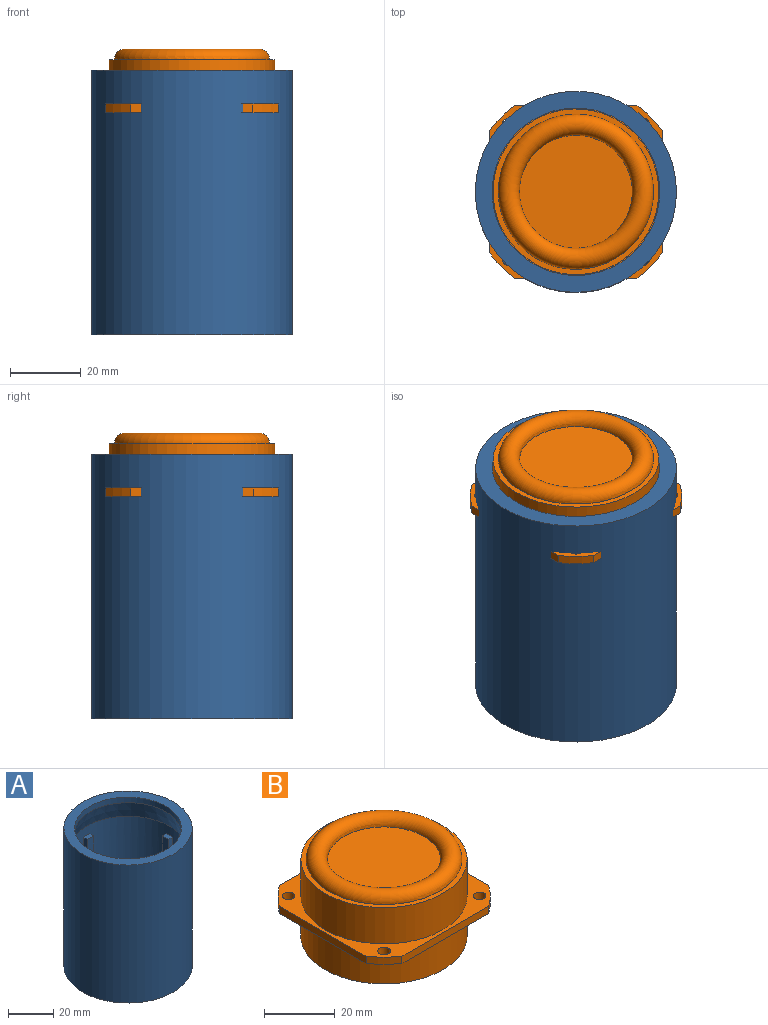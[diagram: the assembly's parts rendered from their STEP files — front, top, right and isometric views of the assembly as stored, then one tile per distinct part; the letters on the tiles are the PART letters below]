
ASSEMBLY  parts=2 mates=1
PART A: 32 faces, bbox 57x57x75 mm
  f0: plane 30x4mm, normal (1,0,0), area 120mm2, adj f5,f10,f11,f28
  f1: plane 30x4mm, normal (0,-1,0), area 120mm2, adj f5,f13,f14,f26
  f2: plane 30x4mm, normal (-1,0,0), area 120mm2, adj f5,f16,f17,f24
  f3: plane 30x4mm, normal (0,1,0), area 120mm2, adj f5,f19,f20,f22
  f4: cylinder r=26mm len=60mm, axis (0,0,-1), area 8920.9mm2, adj f5,f9,f10,f11,f12,f13,f14,f15
  f5: plane 51.85x51.85mm, normal (0,0,1), area 1935.6mm2, adj f0,f1,f2,f3,f4,f7,f10,f11
  f6: cylinder r=28.5mm len=75mm, axis (0,0,-1), area 13430.3mm2, adj f8,f30
  f7: cylinder r=2mm len=4mm, axis (0,0,1), area 37.7mm2, adj f5,f8
  f8: plane 57x57mm, normal (0,0,-1), area 2539.2mm2, adj f6,f7
  f9: plane 4x2.5mm, normal (0,0,1), area 9.9mm2, adj f4,f10,f11,f27
  f10: plane 55x10.92mm, normal (0,-1,0), area 388.3mm2, adj f0,f4,f5,f9,f27,f28
  f11: plane 55x10.92mm, normal (0,1,0), area 388.3mm2, adj f0,f4,f5,f9,f27,f28
  f12: plane 4x2.5mm, normal (0,0,1), area 9.9mm2, adj f4,f13,f14,f25
  f13: plane 55x10.92mm, normal (1,0,0), area 388.3mm2, adj f1,f4,f5,f12,f25,f26
  f14: plane 55x10.92mm, normal (-1,0,0), area 388.3mm2, adj f1,f4,f5,f12,f25,f26
  f15: plane 4x2.5mm, normal (0,0,1), area 9.9mm2, adj f4,f16,f17,f23
  f16: plane 55x10.92mm, normal (0,-1,0), area 388.3mm2, adj f2,f4,f5,f15,f23,f24
  f17: plane 55x10.92mm, normal (0,1,0), area 388.3mm2, adj f2,f4,f5,f15,f23,f24
  f18: plane 4x2.5mm, normal (0,0,1), area 9.9mm2, adj f4,f19,f20,f21
  f19: plane 55x10.92mm, normal (-1,0,0), area 388.3mm2, adj f3,f4,f5,f18,f21,f22
  f20: plane 55x10.92mm, normal (1,0,0), area 388.3mm2, adj f3,f4,f5,f18,f21,f22
  f21: plane 25x4mm, normal (0,1,0), area 100mm2, adj f18,f19,f20,f22
  f22: plane 8.5x4mm, normal (0,0,1), area 34mm2, adj f3,f19,f20,f21
  f23: plane 25x4mm, normal (-1,0,0), area 100mm2, adj f15,f16,f17,f24
  f24: plane 8.5x4mm, normal (0,0,1), area 34mm2, adj f2,f16,f17,f23
  f25: plane 25x4mm, normal (0,-1,0), area 100mm2, adj f12,f13,f14,f26
  f26: plane 8.5x4mm, normal (0,0,1), area 34mm2, adj f1,f13,f14,f25
  f27: plane 25x4mm, normal (1,0,0), area 100mm2, adj f9,f10,f11,f28
  f28: plane 8.5x4mm, normal (0,0,1), area 34mm2, adj f0,f10,f11,f27
  f29: cylinder r=23.75mm len=47.5mm, axis (0,0,-1), area 447.7mm2, adj f30,f31
  f30: plane 57x57mm, normal (0,0,1), area 779.7mm2, adj f6,f29
  f31: cone r=26mm half-angle=14deg, axis (0,0,-1), area 1449.9mm2, adj f4,f29
PART B: 20 faces, bbox 49x49x29.4 mm
  f0: plane 47x47mm, normal (0,0,1), area 214.4mm2, adj f15,f18
  f1: plane 34.63x2.5mm, normal (-1,0,0), area 86.6mm2, adj f2,f12,f13,f14
  f2: cylinder r=30mm len=7.19mm, axis (0,0,-1), area 25.5mm2, adj f1,f3,f13,f14
  f3: plane 34.63x2.5mm, normal (0,-1,0), area 86.6mm2, adj f2,f4,f13,f14
  f4: cylinder r=30mm len=7.19mm, axis (0,0,-1), area 25.5mm2, adj f3,f5,f13,f14
  f5: plane 34.63x2.5mm, normal (1,0,0), area 86.6mm2, adj f4,f6,f13,f14
  f6: cylinder r=30mm len=7.19mm, axis (0,0,-1), area 25.5mm2, adj f5,f7,f13,f14
  f7: plane 34.63x2.5mm, normal (0,1,0), area 86.6mm2, adj f6,f12,f13,f14
  f8: cylinder r=1.8mm len=3.6mm, axis (0,0,-1), area 28.3mm2, adj f13,f14
  f9: cylinder r=1.8mm len=3.6mm, axis (0,0,-1), area 28.3mm2, adj f13,f14
  f10: cylinder r=1.8mm len=3.6mm, axis (0,0,-1), area 28.3mm2, adj f13,f14
  f11: cylinder r=1.8mm len=3.6mm, axis (0,0,-1), area 28.3mm2, adj f13,f14
  f12: cylinder r=30mm len=7.19mm, axis (0,0,-1), area 25.5mm2, adj f1,f7,f13,f14
  f13: plane 49x49mm, normal (0,0,1), area 533.8mm2, adj f1,f2,f3,f4,f5,f6,f7,f8
  f14: plane 49x49mm, normal (0,0,-1), area 533.8mm2, adj f1,f2,f3,f4,f5,f6,f7,f8
  f15: cylinder r=23.5mm len=47mm, axis (0,0,-1), area 1853.1mm2, adj f0,f13
  f16: cylinder r=23.5mm len=47mm, axis (0,0,1), area 1675.9mm2, adj f14,f17
  f17: plane 47x47mm, normal (0,0,-1), area 1734.9mm2, adj f16
  f18: torus R=19mm, axis (0,0,-1), area 1125.1mm2, adj f0,f19
  f19: plane 32x32mm, normal (0,0,1), area 804.2mm2, adj f18
PLACE A t=(0,0,5.67)mm
PLACE B t=(-24.5,-24.5,23.67)mm
MATE cylindrical B.f2 <-> A.f4  axis (0,0,1) through (0,0,18)mm
